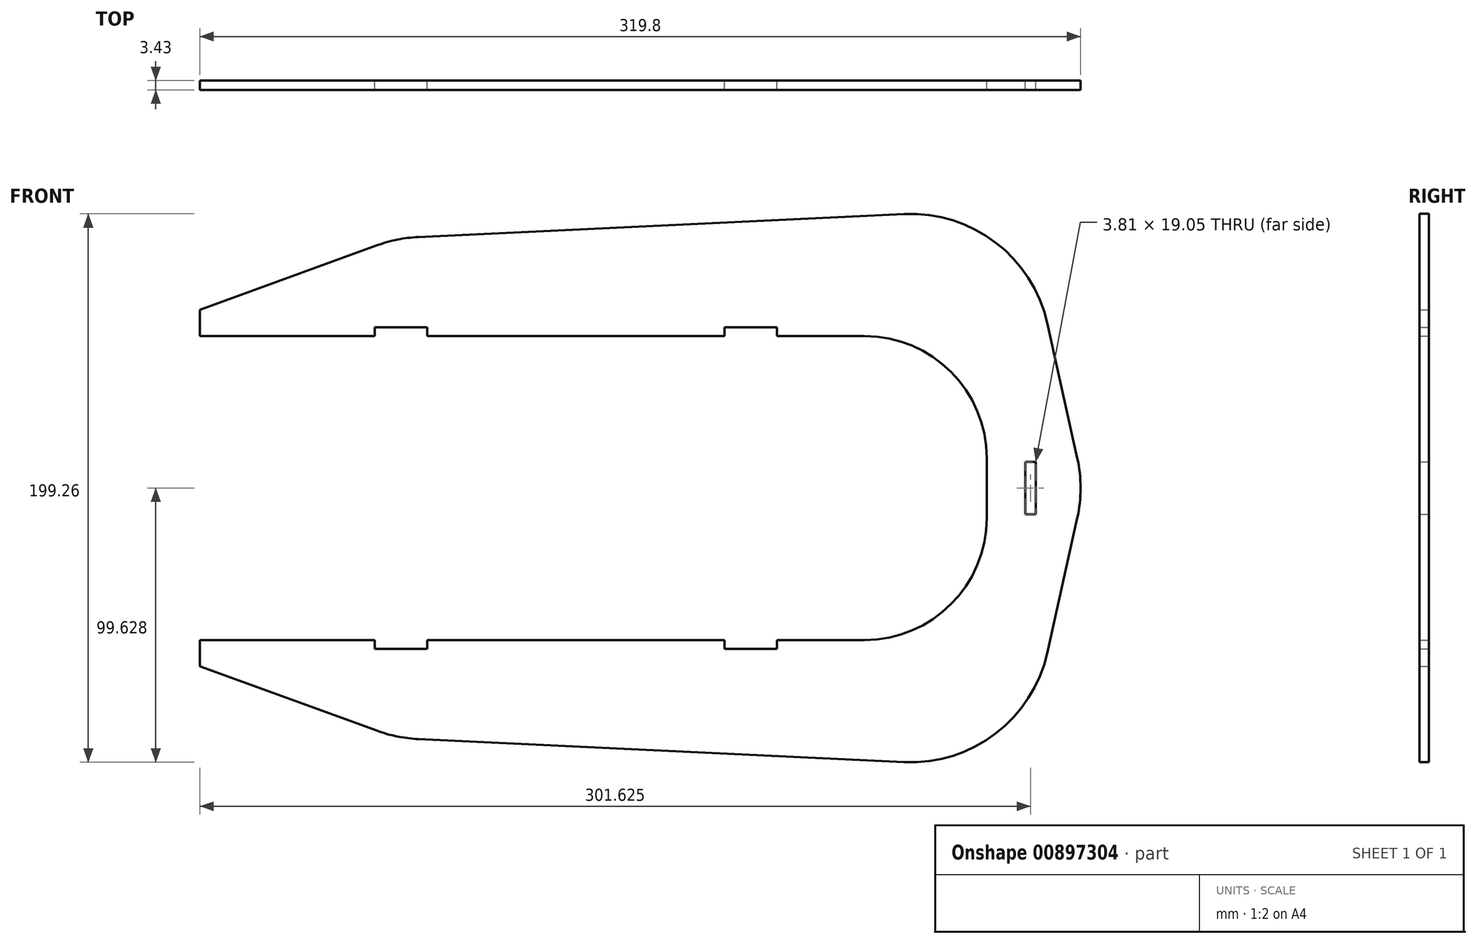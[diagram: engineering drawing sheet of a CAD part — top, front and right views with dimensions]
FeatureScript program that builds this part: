
annotation { "Feature Type Name" : "Feature", "Feature Type Description" : "" }
export const myFeature = defineFeature(function(context is Context, id is Id, definition is map)
    precondition{}
    {
        {
            var Q0;
            Q0=qCreatedBy(makeId("Front.planeOp"),FACE);
            var sketch = newSketch(context, id + "F0", { "sketchPlane" : qUnion([Q0])});
            skLineSegment(sketch, "E0", {"start": v(749.72, 153.97) * mm, "end": v(749.72, 157.15) * mm});
            skLineSegment(sketch, "E1", {"start": v(641.77, 153.97) * mm, "end": v(749.72, 153.97) * mm});
            skLineSegment(sketch, "E2", {"start": v(641.77, 157.15) * mm, "end": v(641.77, 153.97) * mm});
            skLineSegment(sketch, "E3", {"start": v(622.72, 157.15) * mm, "end": v(641.77, 157.15) * mm});
            skLineSegment(sketch, "E4", {"start": v(622.72, 153.97) * mm, "end": v(622.72, 157.15) * mm});
            skLineSegment(sketch, "E5", {"start": v(559.22, 153.97) * mm, "end": v(622.72, 153.97) * mm});
            skLineSegment(sketch, "E6", {"start": v(559.22, 163.5) * mm, "end": v(559.22, 153.97) * mm});
            skLineSegment(sketch, "E7", {"start": v(623.57, 186.92) * mm, "end": v(559.22, 163.5) * mm});
            skArc(sketch, "E8", {"start": v(638.54, 189.93) * mm, "mid": v(630.94, 188.99) * mm, "end": v(623.57, 186.92) * mm});
            skLineSegment(sketch, "E9", {"start": v(814.95, 198.3) * mm, "end": v(638.54, 189.93) * mm});
            skArc(sketch, "E10", {"start": v(866.95, 158.58) * mm, "mid": v(848.2, 187.93) * mm, "end": v(814.95, 198.3) * mm});
            skLineSegment(sketch, "E11", {"start": v(877.8, 109.75) * mm, "end": v(866.95, 158.58) * mm});
            skArc(sketch, "E12", {"start": v(877.8, 87.7) * mm, "mid": v(879.02, 98.73) * mm, "end": v(877.8, 109.75) * mm});
            skLineSegment(sketch, "E13", {"start": v(866.95, 38.87) * mm, "end": v(877.8, 87.7) * mm});
            skArc(sketch, "E14", {"start": v(814.95, -0.84) * mm, "mid": v(848.2, 9.53) * mm, "end": v(866.95, 38.87) * mm});
            skLineSegment(sketch, "E15", {"start": v(638.54, 7.53) * mm, "end": v(814.95, -0.84) * mm});
            skArc(sketch, "E16", {"start": v(623.57, 10.54) * mm, "mid": v(630.94, 8.47) * mm, "end": v(638.54, 7.53) * mm});
            skLineSegment(sketch, "E17", {"start": v(559.22, 33.96) * mm, "end": v(623.57, 10.54) * mm});
            skLineSegment(sketch, "E18", {"start": v(559.22, 43.48) * mm, "end": v(559.22, 33.96) * mm});
            skLineSegment(sketch, "E19", {"start": v(622.72, 43.48) * mm, "end": v(559.22, 43.48) * mm});
            skLineSegment(sketch, "E20", {"start": v(622.72, 40.3) * mm, "end": v(622.72, 43.48) * mm});
            skLineSegment(sketch, "E21", {"start": v(641.77, 40.3) * mm, "end": v(622.72, 40.3) * mm});
            skLineSegment(sketch, "E22", {"start": v(641.77, 43.48) * mm, "end": v(641.77, 40.3) * mm});
            skLineSegment(sketch, "E23", {"start": v(749.72, 43.48) * mm, "end": v(641.77, 43.48) * mm});
            skLineSegment(sketch, "E24", {"start": v(749.72, 40.3) * mm, "end": v(749.72, 43.48) * mm});
            skLineSegment(sketch, "E25", {"start": v(768.77, 40.3) * mm, "end": v(749.72, 40.3) * mm});
            skLineSegment(sketch, "E26", {"start": v(768.77, 43.48) * mm, "end": v(768.77, 40.3) * mm});
            skLineSegment(sketch, "E27", {"start": v(800.52, 43.48) * mm, "end": v(768.77, 43.48) * mm});
            skArc(sketch, "E28", {"start": v(800.52, 43.48) * mm, "mid": v(831.95, 56.5) * mm, "end": v(844.97, 87.93) * mm});
            skLineSegment(sketch, "E29", {"start": v(844.97, 109.52) * mm, "end": v(844.97, 87.93) * mm});
            skArc(sketch, "E30", {"start": v(844.97, 109.52) * mm, "mid": v(831.95, 140.95) * mm, "end": v(800.52, 153.97) * mm});
            skLineSegment(sketch, "E31", {"start": v(768.77, 153.97) * mm, "end": v(800.52, 153.97) * mm});
            skLineSegment(sketch, "E32", {"start": v(768.77, 157.15) * mm, "end": v(768.77, 153.97) * mm});
            skLineSegment(sketch, "E33", {"start": v(749.72, 157.15) * mm, "end": v(768.77, 157.15) * mm});
            skLineSegment(sketch, "E34", {"start": v(862.75, 89.2) * mm, "end": v(858.94, 89.2) * mm});
            skLineSegment(sketch, "E35", {"start": v(862.75, 108.25) * mm, "end": v(862.75, 89.2) * mm});
            skLineSegment(sketch, "E36", {"start": v(858.94, 108.25) * mm, "end": v(862.75, 108.25) * mm});
            skLineSegment(sketch, "E37", {"start": v(858.94, 89.2) * mm, "end": v(858.94, 108.25) * mm});
            skSolve(sketch);
        }
        {
            var Q0;
            Q0 = qSketchRegion(id + "F0", true);
            extrude(context, id + "F1", {"entities" : qUnion([Q0]), "depth" : 3.43 * mm, "offsetDistance" : 25.4 * mm});
        }
    });
